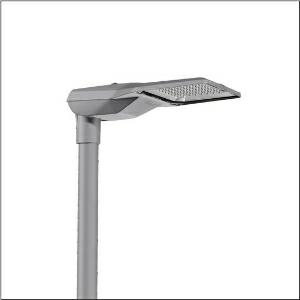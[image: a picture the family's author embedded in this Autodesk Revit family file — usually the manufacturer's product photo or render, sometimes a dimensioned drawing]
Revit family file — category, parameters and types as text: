
# Revit family: streetlight_sl_21_midi___st1_0ab_5xe3m33s08nb_0fd6
name_source: partatom
category: Lighting Fixtures
units: mm (PartAtom-declared; Revit-internal decimal feet)

## family parameters
Cut with Voids When Loaded = No
Host = Face
Light Source = No
Part Type = Normal
Room Calculation Point = No
Round Connector Dimension = Use Diameter
Shared = No

## types (1)
- --- (1 x LED, 19980 lm, 151.2 W, 3000K)
    Apparent Load = 151 VA
    CIE Flux Codes = 40 74 97 100 100
    Color Rendering = 70
    Color Temperature = 3000K
    Default Elevation = 1800 mm
    Description = Streetlight SL 21 midi, mast luminaire, primary light control with lens, of PMMA, primary optical cover: cover, of toughened safety glass, transparent, light distribution: ST1.0aB, light emission: direct distribution, primary light characteristic: asymmetric, installation type: side-entry, post-top, LED, High Power LED, rated luminous flux: 19.980lm, luminous efficacy: 132lm/W, light colour: 730, colour temperature: 3000K, control gear: D4i, control: flexible luminous flux parameterisation, time-dependent luminous flux control, constant luminous flux control, overheat protection, pre-setting: logarithmic dimming characteristic, mains connection: 230..240V, AC, 50/60Hz, start of lifetime: 151W, end of service life: 157W, reduction: 70W, luminaire housing, of diecast aluminium, powder-coated, SITECO metallic grey (DB 702S), corrosivity category C5 high according to DIN EN ISO 12944, please order mast flange separately, inclination adjustable: 0°, 5°, 10°, 15°, sealing non-destructively replaceable, multi-level sealing system, length: 644mm, width: 335mm, height: 110mm, mast flange for spigot size: 42mm (side-entry): 5XC10008XM4, 60/48mm (side-entry/post-top): 5XC10108XM2, 76/60mm (side-entry/post-top): 5XC10108XM1, mounting height: 4..8m, Smart Interface above, protection rating (complete): IP66, insulation class (complete): insulation class II (safety insulation), certification: CE, ENEC, ENEC+, VDE, impact resistance: IK10, permissible operating ambient temperature for outdoor applications: -40..+50°C, standard-compliant lighting for roads and squares, packaging unit: 1 piece

Light Distribution: ST1.0aB
    Height = 111 mm
    Lamp = 1 x LED
    Lamp Light Flux = 19980 lm
    Lamp Power = 151.2 W
    Lamp count = 1
    Length = 644 mm
    Luminous efficacy = 132 lm/W
    Manufacturer = Siteco
    ModVariant = No
    Model = 5XE3M33S08NB
    Number of Poles = 1
    OnlyDefault = Yes
    Power Factor = 1
    Product Name = Streetlight SL 21 midi | ST1.0aB
    Product group = mast luminaire | pylon top
    ProductGroupID = 6100
    Protection Class = Protection class II
    Protection Degree = IP 66
    RLX_Detail_Level = 1
    RLX_Emergency_Light_Flux = 0 lm
    RLX_Emergency_Type = 0
    RLX_Emergency_Type_DB = No
    RlxData = <blob elided: 26901 chars, md5=64049af0>
    Socket = socket
    Standby Power = 0 W
    System Light Flux = 19980 lm
    System Power = 151 W
    Type Comments = factory setting: luminous flux: 100 % | dim-lin: 254 | 802 mA
    Type Image = l_1004302.jpg
    URL = http://relux.com
    VarID = @adj_167623
    Voltage = 0 V
    Weight = 0.00 kg
    Width = 336 mm

## geometry (parser evidence)
native form markers: Blend x4, Sweep x12
no freeform markers — native parametric forms only
